# Revit family: QF_MACON_CB71C-DA
name_source: partatom
category: Equipamento especial
units: mm (PartAtom-declared; Revit-internal decimal feet)

## family parameters
Com base no plano de trabalho = Não
Compartilhado = Não
Corte com vazios quando carregada = Não
Cota do conector redondo = Utilizar diâmetro
Número OmniClass = 23.40.40.14.17.11
Ponto de cálculo do ambiente = Não
Sempre na vertical = Sim
Tipo de parte = Normal
Título OmniClass = Cookers, Ovens, Stoves

## types (2) — shared parameters
Depth = 745,00 mm
Descrição = CHAR BROILER 700HP MACOM 360 GAS
Fabricante = MACOM
Gas Connection Height = 71,00 mm
Gas Pressure = 0,0 bar
Gas Size = 1"
Height = 335,00 mm
Show Clearances = Sim
URL = https://www.acosmacom.com.br
Volume = 0,08 m³
Weight = 34,00 kg
Width = 360,00 mm

## per-type parameters (varying)
| type | Gas Consumption GLP | Gas Consumption GN | Gas Input GLP | Gas Input GN |
| CB71C-G | 0,98 Kg/h | 0,0 m³/h | 44568 Btu/h |  |
| CB71C-N |  | 1,2 m³/h | 0 Btu/h | 11232 Kcal/h |

note: column(s) folded — value = type name in every type: Modelo

## geometry (parser evidence)
native form markers: Sweep x13
no freeform markers — native parametric forms only
